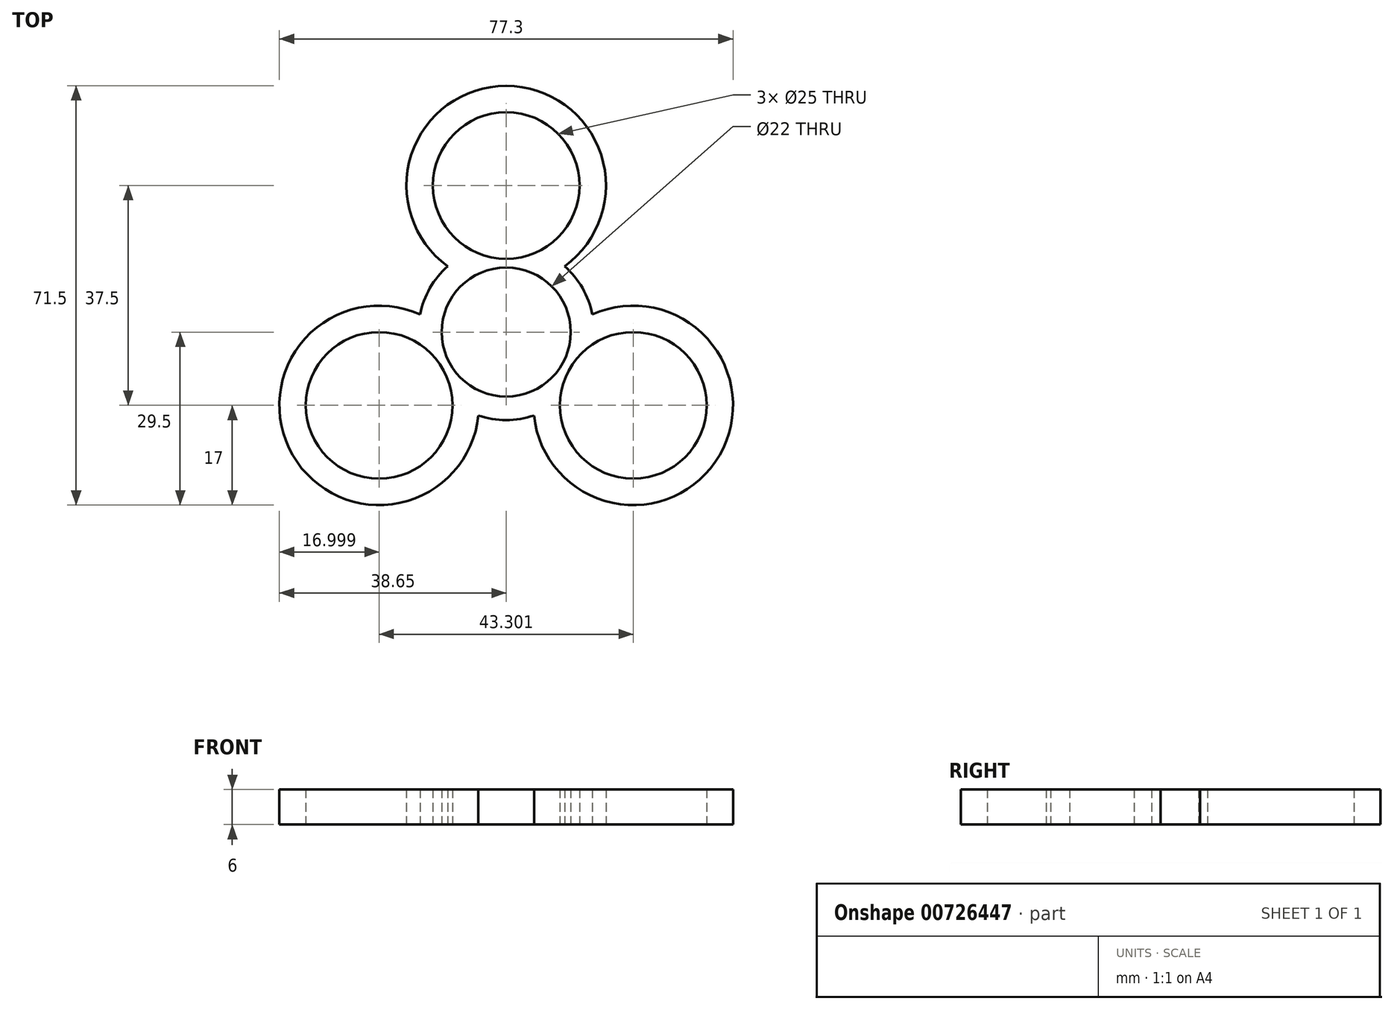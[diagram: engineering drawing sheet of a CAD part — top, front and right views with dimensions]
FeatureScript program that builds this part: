
annotation { "Feature Type Name" : "Feature", "Feature Type Description" : "" }
export const myFeature = defineFeature(function(context is Context, id is Id, definition is map)
    precondition{}
    {
        {
            var Q0;
            Q0=qCreatedBy(makeId("Top.planeOp"),FACE);
            var sketch = newSketch(context, id + "F0", { "sketchPlane" : qUnion([Q0])});
            skArc(sketch, "E0", {"start": v(9.53, 5.5) * mm, "mid": v(0, 11) * mm, "end": v(-9.53, 5.5) * mm});
            skLineSegment(sketch, "E1", {"start": v(0, 0) * mm, "end": v(0, 15) * mm});
            skCircle(sketch, "E2", {"center": v(0, 25) * mm, "radius": 12.5 * mm});
            skArc(sketch, "E3", {"start": v(-9.96, 11.22) * mm, "mid": v(-11.62, 9.48) * mm, "end": v(-13, 7.5) * mm});
            skArc(sketch, "E4", {"start": v(9.96, 11.22) * mm, "mid": v(0, 42) * mm, "end": v(-9.96, 11.22) * mm});
            skArc(sketch, "E5.trimOffspring", {"start": v(13, 7.5) * mm, "mid": v(11.62, 9.48) * mm, "end": v(9.96, 11.22) * mm});
            skCircle(sketch, "E6.1.0", {"center": v(-21.65, -12.5) * mm, "radius": 12.5 * mm});
            skArc(sketch, "E6.1.1", {"start": v(-14.7, 3.01) * mm, "mid": v(-36.37, -21) * mm, "end": v(-4.74, -14.23) * mm});
            skArc(sketch, "E6.1.2", {"start": v(-13, 7.5) * mm, "mid": v(-14.02, 5.32) * mm, "end": v(-14.7, 3.01) * mm});
            skArc(sketch, "E6.1.3", {"start": v(-9.53, 5.5) * mm, "mid": v(-9.53, -5.5) * mm, "end": v(0, -11) * mm});
            skArc(sketch, "E6.1.4", {"start": v(-4.74, -14.23) * mm, "mid": v(-2.4, -14.8) * mm, "end": v(0, -15) * mm});
            skCircle(sketch, "E6.2.0", {"center": v(21.65, -12.5) * mm, "radius": 12.5 * mm});
            skArc(sketch, "E6.2.1", {"start": v(4.74, -14.23) * mm, "mid": v(36.37, -21) * mm, "end": v(14.7, 3.01) * mm});
            skArc(sketch, "E6.2.2", {"start": v(0, -15) * mm, "mid": v(2.4, -14.8) * mm, "end": v(4.74, -14.23) * mm});
            skArc(sketch, "E6.2.3", {"start": v(0, -11) * mm, "mid": v(9.53, -5.5) * mm, "end": v(9.53, 5.5) * mm});
            skArc(sketch, "E6.2.4", {"start": v(14.7, 3.01) * mm, "mid": v(14.02, 5.32) * mm, "end": v(13, 7.5) * mm});
            skSolve(sketch);
        }
        {
            var Q0;
            Q0=makeQuery(id+"F0.imprint","IMPRINT",FACE,{"disambiguationData":[TD([[makeQuery(id+"F0.imprint","IMPRINT",EDGE,{"derivedFrom":sQuery(id+"F0.wireOp",EDGE,"E2")}),-1.0]])]});
            extrude(context, id + "F1", {"entities" : qUnion([Q0]), "depth" : 6 * mm, "offsetDistance" : 25 * mm});
        }
    });
